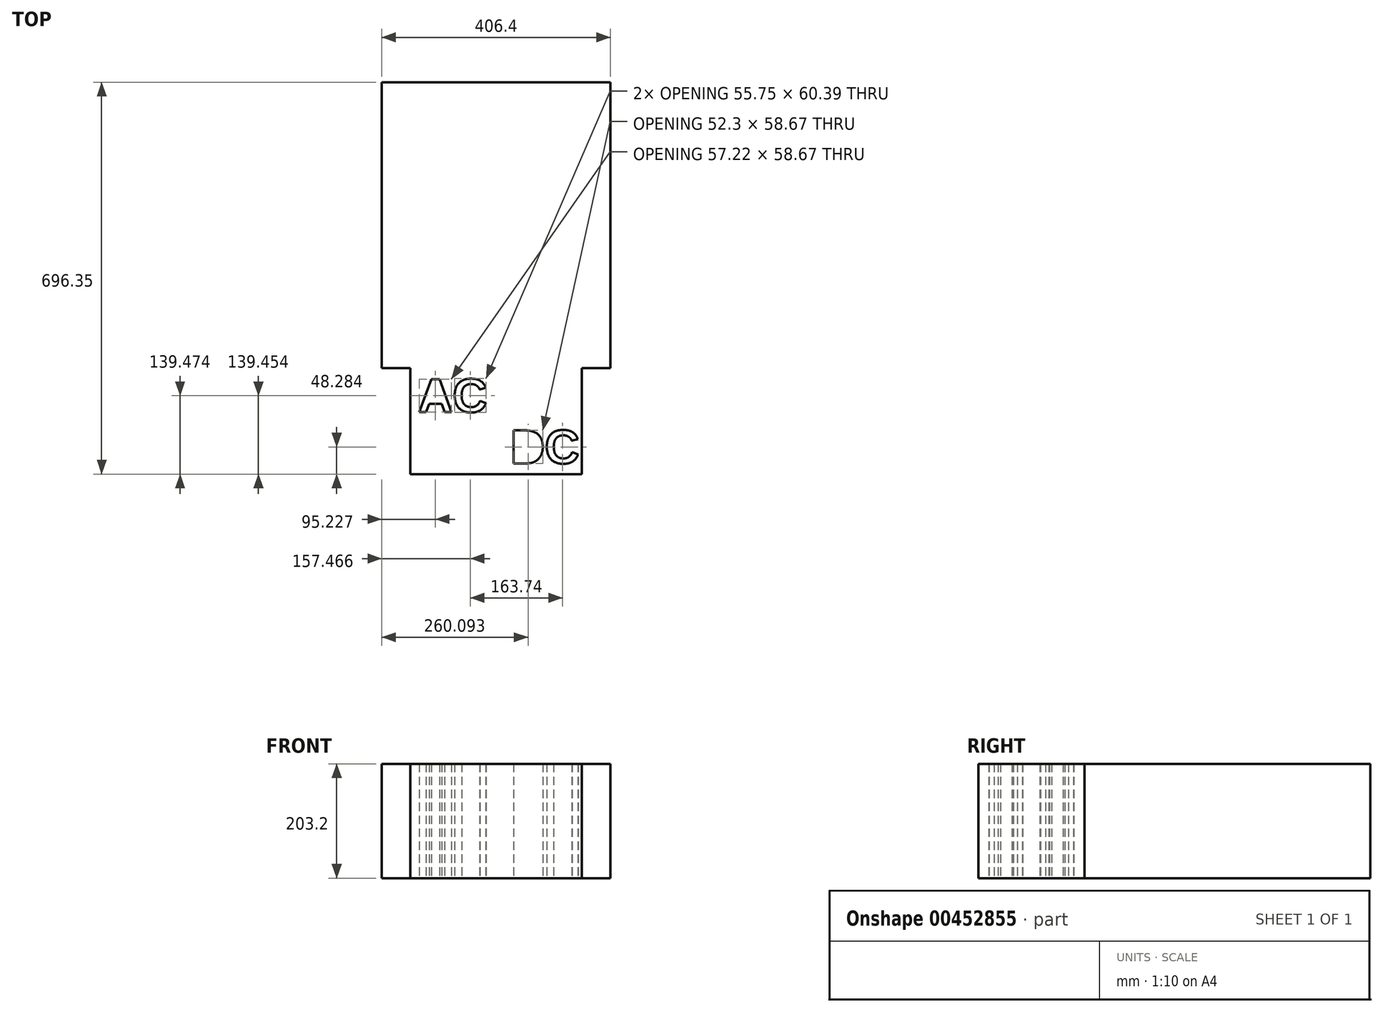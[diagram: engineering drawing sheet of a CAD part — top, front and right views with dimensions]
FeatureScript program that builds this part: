
annotation { "Feature Type Name" : "Feature", "Feature Type Description" : "" }
export const myFeature = defineFeature(function(context is Context, id is Id, definition is map)
    precondition{}
    {
        {
            var Q0;
            Q0=qCreatedBy(makeId("Top.planeOp"),FACE);
            var sketch = newSketch(context, id + "F0", { "sketchPlane" : qUnion([Q0])});
            skLineSegment(sketch, "E0.bottom", {"start": v(-192.38, 225.64) * mm, "end": v(214.02, 225.64) * mm});
            skLineSegment(sketch, "E0.top", {"start": v(-192.38, -282.36) * mm, "end": v(214.02, -282.36) * mm});
            skLineSegment(sketch, "E0.left", {"start": v(-192.38, 225.64) * mm, "end": v(-192.38, -282.36) * mm});
            skLineSegment(sketch, "E0.right", {"start": v(214.02, 225.64) * mm, "end": v(214.02, -282.36) * mm});
            skLineSegment(sketch, "E1.bottom", {"start": v(-141.58, -282.36) * mm, "end": v(163.22, -282.36) * mm});
            skLineSegment(sketch, "E1.top", {"start": v(-141.58, -470.7) * mm, "end": v(163.22, -470.7) * mm});
            skLineSegment(sketch, "E1.left", {"start": v(-141.58, -282.36) * mm, "end": v(-141.58, -470.7) * mm});
            skLineSegment(sketch, "E1.right", {"start": v(163.22, -282.36) * mm, "end": v(163.22, -470.7) * mm});
            skLineSegment(sketch, "E2", {"start": v(-141.58, -470.7) * mm, "end": v(163.22, -282.36) * mm});
            skText(sketch, "E3", { "text": "AC", "fontName": "Arimo-Bold.ttf"});
            skText(sketch, "E4", { "text": "DC", "fontName": "Arimo-Bold.ttf"});
            const initialGuessF0  = {"E3": [-0.12788, -0.36059, 1, 0, 0.0614], "E4": [0.03586, -0.45176, 1, 0, 0.0614]};
            skSetInitialGuess(sketch, initialGuessF0);
            skSolve(sketch);
        }
        {
            var Q0;
            Q0 = qSketchRegion(id + "F0", true);
            extrude(context, id + "F1", {"entities" : qUnion([Q0]), "depth" : 203.2 * mm});
        }
    });
